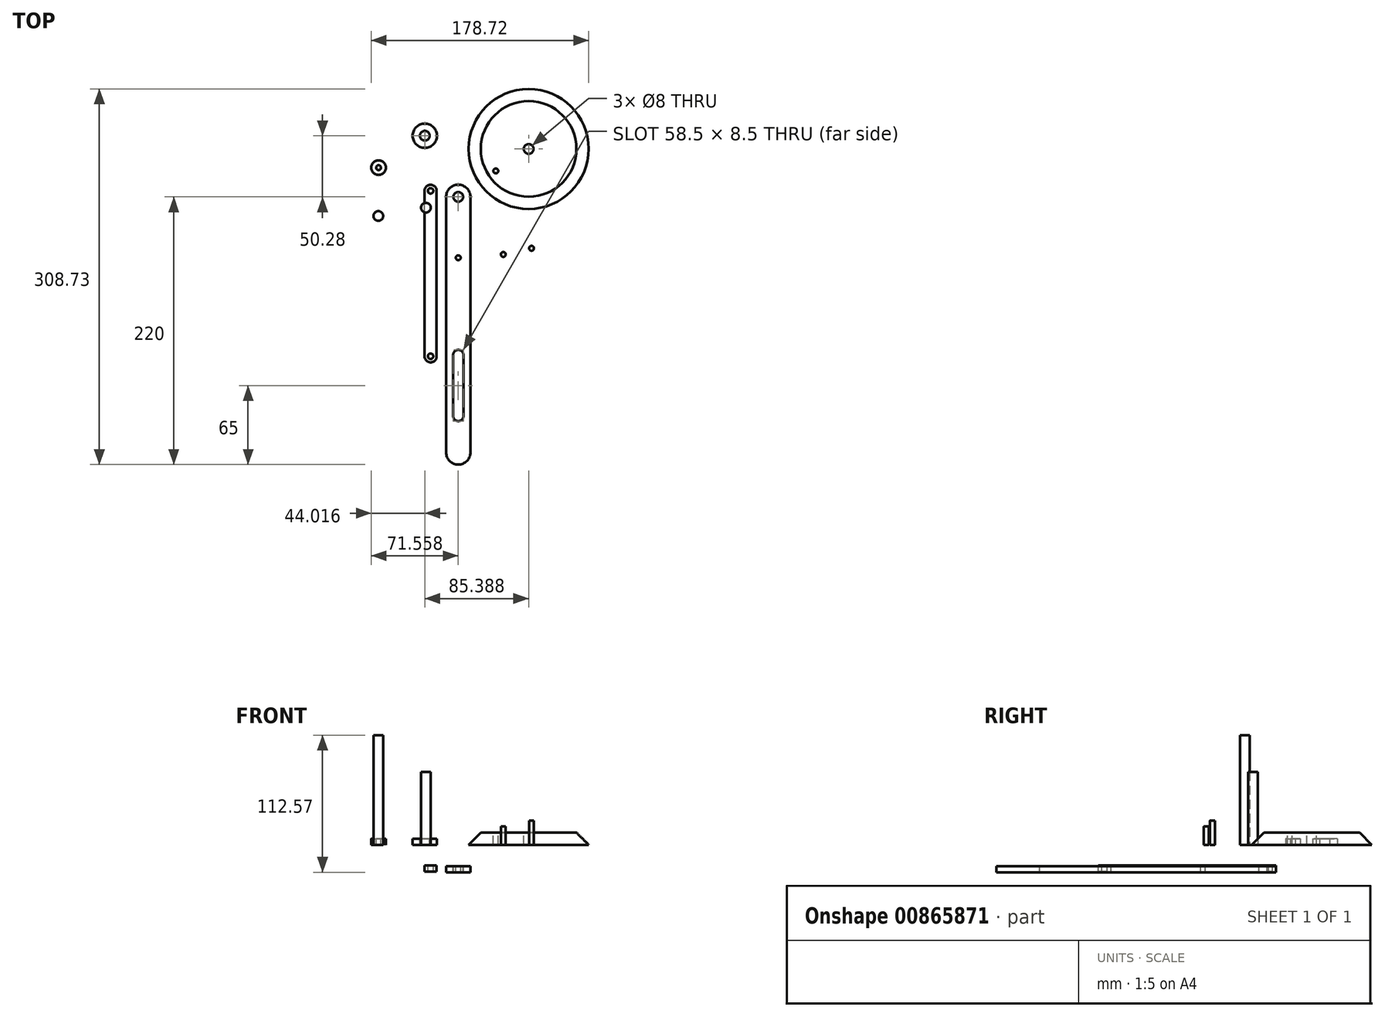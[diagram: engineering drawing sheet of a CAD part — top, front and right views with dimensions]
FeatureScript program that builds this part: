
annotation { "Feature Type Name" : "Feature", "Feature Type Description" : "" }
export const myFeature = defineFeature(function(context is Context, id is Id, definition is map)
    precondition{}
    {
        {
            var Q0;
            Q0=qCreatedBy(makeId("Top.planeOp"),FACE);
            var sketch = newSketch(context, id + "F0", { "sketchPlane" : qUnion([Q0])});
            skCircle(sketch, "E0", {"center": v(35.75, 29.42) * mm, "radius": 49.32 * mm});
            skSolve(sketch);
        }
        {
            var Q0;
            Q0 = qSketchRegion(id + "F0", true);
            extrude(context, id + "F1", {"entities" : qUnion([Q0]), "depth" : 10 * mm, "offsetDistance" : 25 * mm});
        }
        {
            var Q0;
            Q0=makeQuery(id+"F1.opExtrude","CAP_EDGE",EDGE,{"disambiguationData":[OSD([sQuery(id+"F0.wireOp",EDGE,"E0")])],"isStart":false});
            chamfer(context, id + "F2", {"entities" : qUnion([Q0]), "width" : 10 * mm, "tangentPropagation" : true});
        }
        {
            var Q0;
            Q0=makeQuery(id+"F1.opExtrude","CAP_FACE",FACE,{"disambiguationData":[OSD([sQuery(id+"F0.wireOp",EDGE,"E0")])],"isStart":false});
            var sketch = newSketch(context, id + "F3", { "sketchPlane" : qUnion([Q0])});
            skCircle(sketch, "E1", {"center": v(35.75, 29.42) * mm, "radius": 4 * mm});
            skCircle(sketch, "E2", {"center": v(8.74, 11.35) * mm, "radius": 2 * mm});
            skSolve(sketch);
        }
        {
            var Q0;
            Q0 = qSketchRegion(id + "F3", true);
            extrude(context, id + "F4", {"entities" : qUnion([Q0]), "operationType" : NewBodyOperationType.REMOVE, "endBound" : BoundingType.THROUGH_ALL, "oppositeDirection" : true, "depth" : 25 * mm, "offsetDistance" : 25 * mm});
        }
        {
            var Q0;
            Q0=qCreatedBy(makeId("Top.planeOp"),FACE);
            var sketch = newSketch(context, id + "F5", { "sketchPlane" : qUnion([Q0])});
            skCircle(sketch, "E3", {"center": v(-49.63, 40.28) * mm, "radius": 10 * mm});
            skCircle(sketch, "E4", {"center": v(-87.65, 14.03) * mm, "radius": 6 * mm});
            skSolve(sketch);
        }
        {
            var Q0;
            Q0 = qSketchRegion(id + "F5", true);
            extrude(context, id + "F6", {"entities" : qUnion([Q0]), "depth" : 5 * mm, "offsetDistance" : 25 * mm});
        }
        {
            var Q0;
            Q0=makeQuery(id+"F6.opExtrude","CAP_FACE",FACE,{"disambiguationData":[OSD([sQuery(id+"F5.wireOp",EDGE,"E3")])],"isStart":false});
            var sketch = newSketch(context, id + "F7", { "sketchPlane" : qUnion([Q0])});
            skCircle(sketch, "E5", {"center": v(-49.63, 40.28) * mm, "radius": 4 * mm});
            skSolve(sketch);
        }
        {
            var Q0;
            Q0 = qSketchRegion(id + "F7", true);
            extrude(context, id + "F8", {"entities" : qUnion([Q0]), "operationType" : NewBodyOperationType.REMOVE, "endBound" : BoundingType.THROUGH_ALL, "oppositeDirection" : true, "depth" : 25 * mm, "offsetDistance" : 25 * mm});
        }
        {
            var Q0;
            Q0=qCreatedBy(makeId("Top.planeOp"),FACE);
            var sketch = newSketch(context, id + "F9", { "sketchPlane" : qUnion([Q0])});
            skCircle(sketch, "E6", {"center": v(-48.73, -18.86) * mm, "radius": 4 * mm});
            skSolve(sketch);
        }
        {
            var Q0;
            Q0 = qSketchRegion(id + "F9", true);
            extrude(context, id + "F10", {"entities" : qUnion([Q0]), "depth" : 60 * mm, "offsetDistance" : 25 * mm});
        }
        {
            var Q0;
            Q0=makeQuery(id+"F6.opExtrude","CAP_FACE",FACE,{"disambiguationData":[OSD([sQuery(id+"F5.wireOp",EDGE,"E4")])],"isStart":false});
            var sketch = newSketch(context, id + "F11", { "sketchPlane" : qUnion([Q0])});
            skCircle(sketch, "E7", {"center": v(-87.65, 14.03) * mm, "radius": 2 * mm});
            skSolve(sketch);
        }
        {
            var Q0;
            Q0 = qSketchRegion(id + "F11", true);
            extrude(context, id + "F12", {"entities" : qUnion([Q0]), "operationType" : NewBodyOperationType.REMOVE, "endBound" : BoundingType.THROUGH_ALL, "oppositeDirection" : true, "depth" : 25 * mm, "offsetDistance" : 25 * mm});
        }
        {
            var Q0;
            Q0=qCreatedBy(makeId("Front.planeOp"),FACE);
            var sketch = newSketch(context, id + "F13", { "sketchPlane" : qUnion([Q0])});
            skLineSegment(sketch, "E8.bottom", {"start": v(-49.87, -17.1) * mm, "end": v(-39.87, -17.1) * mm});
            skLineSegment(sketch, "E8.top", {"start": v(-49.87, -22.1) * mm, "end": v(-39.87, -22.1) * mm});
            skLineSegment(sketch, "E8.left", {"start": v(-49.87, -17.1) * mm, "end": v(-49.87, -22.1) * mm});
            skLineSegment(sketch, "E8.right", {"start": v(-39.87, -17.1) * mm, "end": v(-39.87, -22.1) * mm});
            skSolve(sketch);
        }
        {
            var Q0;
            Q0 = qSketchRegion(id + "F13", true);
            extrude(context, id + "F14", {"entities" : qUnion([Q0]), "depth" : 146 * mm, "offsetDistance" : 25 * mm});
        }
        {
            var Q0;
            Q0=makeQuery(id+"F14.opExtrude","CAP_EDGE",EDGE,{"disambiguationData":[OSD([sQuery(id+"F13.wireOp",EDGE,"E8.left")])],"isStart":false});
            var Q1;
            Q1=makeQuery(id+"F14.opExtrude","CAP_EDGE",EDGE,{"disambiguationData":[OSD([sQuery(id+"F13.wireOp",EDGE,"E8.right")])],"isStart":false});
            var Q2;
            Q2=makeQuery(id+"F14.opExtrude","CAP_EDGE",EDGE,{"disambiguationData":[OSD([sQuery(id+"F13.wireOp",EDGE,"E8.right")])],"isStart":true});
            var Q3;
            Q3=makeQuery(id+"F14.opExtrude","CAP_EDGE",EDGE,{"disambiguationData":[OSD([sQuery(id+"F13.wireOp",EDGE,"E8.left")])],"isStart":true});
            fillet(context, id + "F15", {"entities" : qUnion([Q0, Q1, Q2, Q3]), "radius" : 5 * mm, "tangentPropagation" : true, "allowEdgeOverflow" : false});
        }
        {
            var Q0;
            Q0=makeQuery(id+"F14.opExtrude","SWEPT_FACE",FACE,{"disambiguationData":[OSD([sQuery(id+"F13.wireOp",EDGE,"E8.bottom")])]});
            var sketch = newSketch(context, id + "F16", { "sketchPlane" : qUnion([Q0])});
            skCircle(sketch, "E9", {"center": v(-44.87, -5) * mm, "radius": 2.25 * mm});
            skCircle(sketch, "E10", {"center": v(-44.87, -141) * mm, "radius": 2.25 * mm});
            skSolve(sketch);
        }
        {
            var Q0;
            Q0 = qSketchRegion(id + "F16", true);
            extrude(context, id + "F17", {"entities" : qUnion([Q0]), "operationType" : NewBodyOperationType.REMOVE, "endBound" : BoundingType.THROUGH_ALL, "oppositeDirection" : true, "depth" : 25 * mm, "offsetDistance" : 25 * mm});
        }
        {
            var Q0;
            Q0=qCreatedBy(makeId("Front.planeOp"),FACE);
            var sketch = newSketch(context, id + "F18", { "sketchPlane" : qUnion([Q0])});
            skLineSegment(sketch, "E11.bottom", {"start": v(-32.1, -17.57) * mm, "end": v(-12.1, -17.57) * mm});
            skLineSegment(sketch, "E11.top", {"start": v(-32.1, -22.57) * mm, "end": v(-12.1, -22.57) * mm});
            skLineSegment(sketch, "E11.left", {"start": v(-32.1, -17.57) * mm, "end": v(-32.1, -22.57) * mm});
            skLineSegment(sketch, "E11.right", {"start": v(-12.1, -17.57) * mm, "end": v(-12.1, -22.57) * mm});
            skSolve(sketch);
        }
        {
            var Q0;
            Q0 = qSketchRegion(id + "F18", true);
            extrude(context, id + "F19", {"entities" : qUnion([Q0]), "depth" : 230 * mm, "offsetDistance" : 25 * mm});
        }
        {
            var Q0;
            Q0=makeQuery(id+"F19.opExtrude","CAP_EDGE",EDGE,{"disambiguationData":[OSD([sQuery(id+"F18.wireOp",EDGE,"E11.left")])],"isStart":false});
            var Q1;
            Q1=makeQuery(id+"F19.opExtrude","CAP_EDGE",EDGE,{"disambiguationData":[OSD([sQuery(id+"F18.wireOp",EDGE,"E11.right")])],"isStart":false});
            var Q2;
            Q2=makeQuery(id+"F19.opExtrude","CAP_EDGE",EDGE,{"disambiguationData":[OSD([sQuery(id+"F18.wireOp",EDGE,"E11.left")])],"isStart":true});
            var Q3;
            Q3=makeQuery(id+"F19.opExtrude","CAP_EDGE",EDGE,{"disambiguationData":[OSD([sQuery(id+"F18.wireOp",EDGE,"E11.right")])],"isStart":true});
            fillet(context, id + "F20", {"entities" : qUnion([Q0, Q1, Q2, Q3]), "radius" : 10 * mm, "tangentPropagation" : true, "allowEdgeOverflow" : false});
        }
        {
            var Q0;
            Q0=makeQuery(id+"F19.opExtrude","SWEPT_FACE",FACE,{"disambiguationData":[OSD([sQuery(id+"F18.wireOp",EDGE,"E11.bottom")])]});
            var sketch = newSketch(context, id + "F21", { "sketchPlane" : qUnion([Q0])});
            skCircle(sketch, "E12", {"center": v(-22.1, -10) * mm, "radius": 4 * mm});
            skCircle(sketch, "E13", {"center": v(-22.1, -140) * mm, "radius": 4.25 * mm});
            skCircle(sketch, "E14", {"center": v(-22.1, -190) * mm, "radius": 4.25 * mm});
            skPoint(sketch, "E14.centerSnap0", {"position": v(-22.1, 0) * mm});
            skLineSegment(sketch, "E15", {"start": v(-26.34, -140) * mm, "end": v(-26.34, -190) * mm});
            skLineSegment(sketch, "E16", {"start": v(-17.84, -140) * mm, "end": v(-17.84, -190) * mm});
            skSolve(sketch);
        }
        {
            var Q0;
            Q0 = qSketchRegion(id + "F21", true);
            extrude(context, id + "F22", {"entities" : qUnion([Q0]), "operationType" : NewBodyOperationType.REMOVE, "endBound" : BoundingType.THROUGH_ALL, "oppositeDirection" : true, "depth" : 25 * mm, "offsetDistance" : 25 * mm});
        }
        {
            var Q0;
            Q0=makeQuery(id+"F19.opExtrude","SWEPT_FACE",FACE,{"disambiguationData":[OSD([sQuery(id+"F18.wireOp",EDGE,"E11.bottom")])]});
            var sketch = newSketch(context, id + "F23", { "sketchPlane" : qUnion([Q0])});
            skCircle(sketch, "E17", {"center": v(-22.1, -60) * mm, "radius": 2 * mm});
            skPoint(sketch, "E17.centerSnap0", {"position": v(-22.1, 0) * mm});
            skSolve(sketch);
        }
        {
            var Q0;
            Q0 = qSketchRegion(id + "F23", true);
            extrude(context, id + "F24", {"entities" : qUnion([Q0]), "operationType" : NewBodyOperationType.REMOVE, "endBound" : BoundingType.THROUGH_ALL, "oppositeDirection" : true, "depth" : 15 * mm, "offsetDistance" : 25 * mm});
        }
        {
            var Q0;
            Q0=qCreatedBy(makeId("Top.planeOp"),FACE);
            var sketch = newSketch(context, id + "F25", { "sketchPlane" : qUnion([Q0])});
            skCircle(sketch, "E18", {"center": v(-87.82, -25.64) * mm, "radius": 4 * mm});
            skSolve(sketch);
        }
        {
            var Q0;
            Q0 = qSketchRegion(id + "F25", true);
            extrude(context, id + "F26", {"entities" : qUnion([Q0]), "depth" : 90 * mm, "offsetDistance" : 25 * mm});
        }
        {
            var Q0;
            Q0=qCreatedBy(makeId("Top.planeOp"),FACE);
            var sketch = newSketch(context, id + "F27", { "sketchPlane" : qUnion([Q0])});
            skCircle(sketch, "E19", {"center": v(14.9, -57.34) * mm, "radius": 2 * mm});
            skSolve(sketch);
        }
        {
            var Q0;
            Q0 = qSketchRegion(id + "F27", true);
            extrude(context, id + "F28", {"entities" : qUnion([Q0]), "depth" : 15 * mm, "offsetDistance" : 25 * mm});
        }
        {
            var Q0;
            Q0=qCreatedBy(makeId("Top.planeOp"),FACE);
            var sketch = newSketch(context, id + "F29", { "sketchPlane" : qUnion([Q0])});
            skCircle(sketch, "E20", {"center": v(38.12, -52.27) * mm, "radius": 2 * mm});
            skSolve(sketch);
        }
        {
            var Q0;
            Q0 = qSketchRegion(id + "F29", true);
            extrude(context, id + "F30", {"entities" : qUnion([Q0]), "depth" : 20 * mm, "offsetDistance" : 25 * mm});
        }
    });
